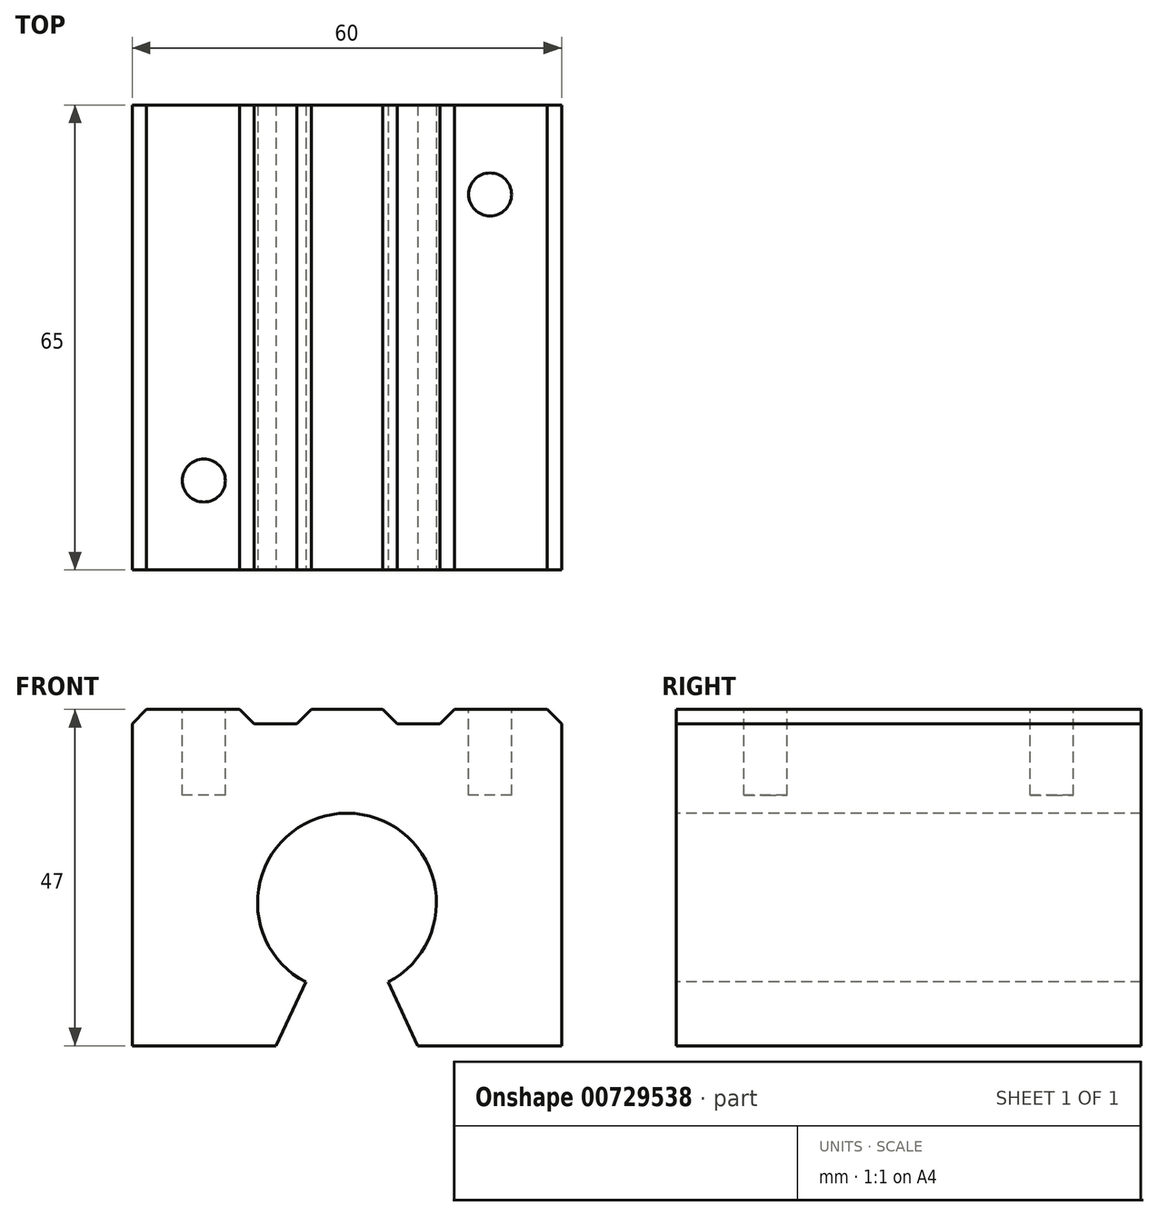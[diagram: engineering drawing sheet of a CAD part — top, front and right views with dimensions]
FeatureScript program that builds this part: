
annotation { "Feature Type Name" : "Feature", "Feature Type Description" : "" }
export const myFeature = defineFeature(function(context is Context, id is Id, definition is map)
    precondition{}
    {
        {
            var Q0;
            Q0=qCreatedBy(makeId("Front.planeOp"),FACE);
            var sketch = newSketch(context, id + "F0", { "sketchPlane" : qUnion([Q0])});
            skArc(sketch, "E0", {"start": v(5.75, -11.1) * mm, "mid": v(0, 12.5) * mm, "end": v(-5.75, -11.1) * mm});
            skLineSegment(sketch, "E1", {"start": v(0, 33.95) * mm, "end": v(0, -22.88) * mm, "construction": true});
            skLineSegment(sketch, "E2", {"start": v(0, 27) * mm, "end": v(5, 27) * mm});
            skLineSegment(sketch, "E3", {"start": v(30, 27) * mm, "end": v(30, -11.1) * mm});
            skLineSegment(sketch, "E4.MirrorCS", {"start": v(0, 27) * mm, "end": v(-5, 27) * mm});
            skLineSegment(sketch, "E5.MirrorCS", {"start": v(-30, 27) * mm, "end": v(-30, -11.1) * mm});
            skPoint(sketch, "E6.orphan", {"position": v(0, 30.01) * mm});
            skLineSegment(sketch, "E7", {"start": v(5, 27) * mm, "end": v(7, 25) * mm});
            skLineSegment(sketch, "E8", {"start": v(7, 25) * mm, "end": v(13, 25) * mm});
            skLineSegment(sketch, "E9", {"start": v(13, 25) * mm, "end": v(15, 27) * mm});
            skLineSegment(sketch, "E10.MirrorCS", {"start": v(-5, 27) * mm, "end": v(-7, 25) * mm});
            skLineSegment(sketch, "E11.MirrorCS", {"start": v(-7, 25) * mm, "end": v(-13, 25) * mm});
            skLineSegment(sketch, "E12.MirrorCS", {"start": v(-13, 25) * mm, "end": v(-15, 27) * mm});
            skLineSegment(sketch, "E13.trimOffspring", {"start": v(15, 27) * mm, "end": v(30, 27) * mm});
            skLineSegment(sketch, "E14.trimOffspring", {"start": v(-15, 27) * mm, "end": v(-30, 27) * mm});
            skLineSegment(sketch, "E15", {"start": v(-30, -11.1) * mm, "end": v(-30, -20) * mm});
            skLineSegment(sketch, "E16", {"start": v(-30, -20) * mm, "end": v(-9.9, -20) * mm});
            skLineSegment(sketch, "E17", {"start": v(30, -20) * mm, "end": v(30, -11.1) * mm});
            skLineSegment(sketch, "E18", {"start": v(-5.75, -11.1) * mm, "end": v(-9.9, -20) * mm});
            skLineSegment(sketch, "E19.MirrorCS", {"start": v(5.75, -11.1) * mm, "end": v(9.9, -20) * mm});
            skPoint(sketch, "E20.end.orphan", {"position": v(5.75, -11.1) * mm});
            skLineSegment(sketch, "E21.trimOffspring", {"start": v(9.9, -20) * mm, "end": v(30, -20) * mm});
            skPoint(sketch, "E22.MirrorCS.start.orphan", {"position": v(-30, -11.1) * mm});
            skSolve(sketch);
        }
        {
            var Q0;
            Q0=makeQuery(id+"F0.imprint","IMPRINT",FACE,{"disambiguationData":[TD([[makeQuery(id+"F0.imprint","IMPRINT",EDGE,{"derivedFrom":sQuery(id+"F0.wireOp",EDGE,"E0")}),-1.0]])]});
            extrude(context, id + "F1", {"entities" : qUnion([Q0]), "oppositeDirection" : true, "depth" : 65 * mm, "offsetDistance" : 25 * mm});
        }
        {
            var Q0;
            Q0=makeQuery(id+"F1.opExtrude","SWEPT_FACE",FACE,{"disambiguationData":[OSD([sQuery(id+"F0.wireOp",EDGE,"E2"),sQuery(id+"F0.wireOp",EDGE,"E4.MirrorCS")])]});
            var sketch = newSketch(context, id + "F2", { "sketchPlane" : qUnion([Q0])});
            skLineSegment(sketch, "E23.bottom", {"start": v(0, 52.5) * mm, "end": v(20, 52.5) * mm, "construction": true});
            skLineSegment(sketch, "E23.right", {"start": v(20, 52.5) * mm, "end": v(20, 32.5) * mm, "construction": true});
            skCircle(sketch, "E24", {"center": v(20, 52.5) * mm, "radius": 3 * mm});
            skLineSegment(sketch, "E25", {"start": v(0, 67.54) * mm, "end": v(0, -5.3) * mm, "construction": true});
            skLineSegment(sketch, "E26", {"start": v(-43.18, 32.5) * mm, "end": v(57.19, 32.5) * mm, "construction": true});
            skCircle(sketch, "E27.MirrorC", {"center": v(-20, 52.5) * mm, "radius": 3 * mm});
            skCircle(sketch, "E28.MirrorC", {"center": v(-20, 12.5) * mm, "radius": 3 * mm});
            skCircle(sketch, "E29.MirrorC", {"center": v(20, 12.5) * mm, "radius": 3 * mm});
            skSolve(sketch);
        }
        {
            var Q0;
            Q0=makeQuery(id+"F1.opExtrude","SWEPT_EDGE",EDGE,{"disambiguationData":[OSD([sQuery(id+"F0.wireOp",EDGE,"E3"),sQuery(id+"F0.wireOp",EDGE,"E13.trimOffspring")])]});
            var Q1;
            Q1=makeQuery(id+"F1.opExtrude","SWEPT_EDGE",EDGE,{"disambiguationData":[OSD([sQuery(id+"F0.wireOp",EDGE,"E5.MirrorCS"),sQuery(id+"F0.wireOp",EDGE,"E14.trimOffspring")])]});
            chamfer(context, id + "F3", {"entities" : qUnion([Q0, Q1]), "width" : 2 * mm, "tangentPropagation" : true});
        }
        {
            var Q0;
            Q0=makeQuery(id+"F2.imprint","IMPRINT",FACE,{"disambiguationData":[TD([[makeQuery(id+"F2.imprint","IMPRINT",EDGE,{"derivedFrom":sQuery(id+"F2.wireOp",EDGE,"E27.MirrorC")}),-1.0]])]});
            var Q1;
            Q1=makeQuery(id+"F2.imprint","IMPRINT",FACE,{"disambiguationData":[TD([[makeQuery(id+"F2.imprint","IMPRINT",EDGE,{"derivedFrom":sQuery(id+"F2.wireOp",EDGE,"E28.MirrorC")}),1.0]])]});
            var Q2;
            Q2=makeQuery(id+"F2.imprint","IMPRINT",FACE,{"disambiguationData":[TD([[makeQuery(id+"F2.imprint","IMPRINT",EDGE,{"derivedFrom":sQuery(id+"F2.wireOp",EDGE,"E24")}),1.0]])]});
            var Q3;
            Q3=makeQuery(id+"F2.imprint","IMPRINT",FACE,{"disambiguationData":[TD([[makeQuery(id+"F2.imprint","IMPRINT",EDGE,{"derivedFrom":sQuery(id+"F2.wireOp",EDGE,"E29.MirrorC")}),-1.0]])]});
            extrude(context, id + "F4", {"entities" : qUnion([Q0, Q1, Q2, Q3]), "operationType" : NewBodyOperationType.REMOVE, "oppositeDirection" : true, "depth" : 12 * mm, "offsetDistance" : 25 * mm});
        }
    });
